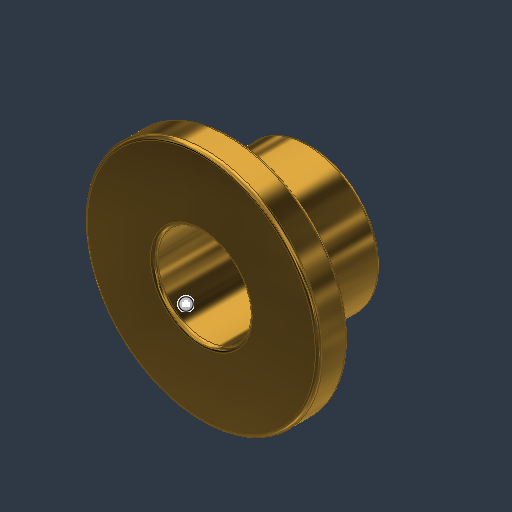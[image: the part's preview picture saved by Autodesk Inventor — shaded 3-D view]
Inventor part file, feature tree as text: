
AUTODESK INVENTOR PART (.ipt)
format: ipt  version: 2024.3 (Build 283343000, 343)  size: 177,152 bytes
history: native  units: mm (DEFAULTED — no unit token found)
features: revolve x1, fillet x1, sketch x1
ambient origin geometry x8: Origin, YZ Plane, XZ Plane, XY Plane, X Axis, Y Axis, Z Axis, Center Point
bodies: Solid1 (feature_tree)
feature tree (3):
  revolve  "Revolution1"  [1 undecoded]
  fillet  "Fillet1"  Radius=9.525mm
  sketch  "Sketch2"  dims[d0=2.032mm d1=6.35mm d2=9.525mm d5=15.875mm d6=90.0deg d7=0.254mm d8=0.0mm d9=7.366mm]
note: 1 required parameter value undecoded (feature->parameter linkage not recoverable at this tier; creation-order binding heuristic only, values carry confidence <= 0.55)
